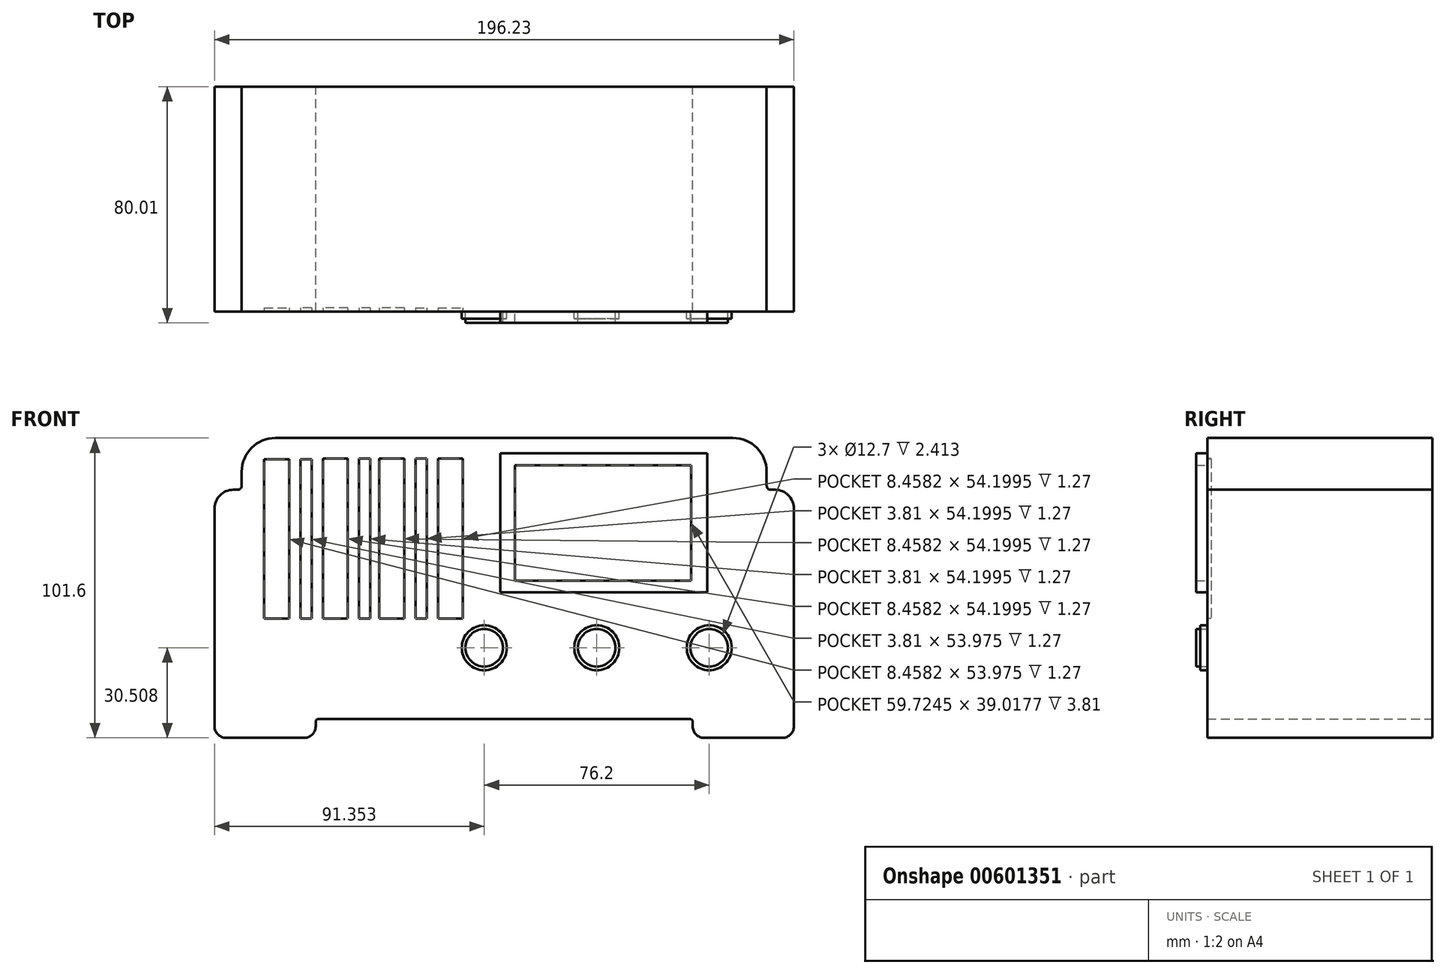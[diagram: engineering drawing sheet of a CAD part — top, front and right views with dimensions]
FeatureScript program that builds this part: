
annotation { "Feature Type Name" : "Feature", "Feature Type Description" : "" }
export const myFeature = defineFeature(function(context is Context, id is Id, definition is map)
    precondition{}
    {
        {
            var Q0;
            Q0=qCreatedBy(makeId("Front.planeOp"),FACE);
            var sketch = newSketch(context, id + "F0", { "sketchPlane" : qUnion([Q0])});
            skLineSegment(sketch, "E0", {"start": v(-84.76, 56.27) * mm, "end": v(93.04, 56.27) * mm});
            skLineSegment(sketch, "E1", {"start": v(-84.76, 56.27) * mm, "end": v(-84.76, -45.33) * mm});
            skLineSegment(sketch, "E2", {"start": v(93.04, 56.27) * mm, "end": v(93.04, -45.33) * mm});
            skLineSegment(sketch, "E3", {"start": v(-84.76, 38.7) * mm, "end": v(-93.97, 38.7) * mm});
            skLineSegment(sketch, "E4", {"start": v(-93.97, 38.7) * mm, "end": v(-93.97, -45.33) * mm});
            skLineSegment(sketch, "E5", {"start": v(-93.97, -45.33) * mm, "end": v(-84.76, -45.33) * mm});
            skLineSegment(sketch, "E6", {"start": v(93.04, 38.7) * mm, "end": v(102.26, 38.7) * mm});
            skLineSegment(sketch, "E7", {"start": v(102.26, 38.7) * mm, "end": v(102.26, -45.33) * mm});
            skLineSegment(sketch, "E8", {"start": v(102.26, -45.33) * mm, "end": v(93.04, -45.33) * mm});
            skLineSegment(sketch, "E9", {"start": v(-84.76, -45.33) * mm, "end": v(-59.72, -45.33) * mm});
            skLineSegment(sketch, "E10", {"start": v(-59.72, -45.33) * mm, "end": v(-59.72, -39) * mm});
            skLineSegment(sketch, "E11", {"start": v(93.04, -45.33) * mm, "end": v(68, -45.33) * mm});
            skLineSegment(sketch, "E12", {"start": v(68, -45.33) * mm, "end": v(68, -39) * mm});
            skLineSegment(sketch, "E13", {"start": v(68, -39) * mm, "end": v(-59.72, -39) * mm});
            skSolve(sketch);
        }
        {
            var Q0;
            Q0 = qSketchRegion(id + "F0", true);
            extrude(context, id + "F1", {"entities" : qUnion([Q0]), "depth" : 76.2 * mm, "offsetDistance" : 25.4 * mm});
        }
        {
            var Q0;
            Q0=makeQuery(id+"F1.opExtrude","CAP_FACE",FACE,{"disambiguationData":[OSD([sQuery(id+"F0.wireOp",EDGE,"E0"),sQuery(id+"F0.wireOp",EDGE,"E1"),sQuery(id+"F0.wireOp",EDGE,"E2"),sQuery(id+"F0.wireOp",EDGE,"E3"),sQuery(id+"F0.wireOp",EDGE,"E4"),sQuery(id+"F0.wireOp",EDGE,"E5"),sQuery(id+"F0.wireOp",EDGE,"E6"),sQuery(id+"F0.wireOp",EDGE,"E7"),sQuery(id+"F0.wireOp",EDGE,"E8"),sQuery(id+"F0.wireOp",EDGE,"E9"),sQuery(id+"F0.wireOp",EDGE,"E10"),sQuery(id+"F0.wireOp",EDGE,"E11"),sQuery(id+"F0.wireOp",EDGE,"E12"),sQuery(id+"F0.wireOp",EDGE,"E13")])],"isStart":false});
            var sketch = newSketch(context, id + "F2", { "sketchPlane" : qUnion([Q0])});
            skCircle(sketch, "E14", {"center": v(-2.62, -14.82) * mm, "radius": 6.35 * mm});
            skCircle(sketch, "E15", {"center": v(35.48, -14.82) * mm, "radius": 6.35 * mm});
            skCircle(sketch, "E16", {"center": v(73.58, -14.82) * mm, "radius": 6.35 * mm});
            skCircle(sketch, "E17", {"center": v(-2.62, -14.82) * mm, "radius": 7.62 * mm});
            skCircle(sketch, "E18", {"center": v(35.48, -14.82) * mm, "radius": 7.62 * mm});
            skCircle(sketch, "E19", {"center": v(73.58, -14.82) * mm, "radius": 7.62 * mm});
            skLineSegment(sketch, "E20", {"start": v(-77.16, 49.02) * mm, "end": v(-77.16, -4.96) * mm});
            skLineSegment(sketch, "E21", {"start": v(-77.16, 49.02) * mm, "end": v(-68.7, 49.02) * mm});
            skLineSegment(sketch, "E22", {"start": v(-68.7, 49.02) * mm, "end": v(-68.7, -4.96) * mm});
            skLineSegment(sketch, "E23", {"start": v(-68.7, -4.96) * mm, "end": v(-77.16, -4.96) * mm});
            skLineSegment(sketch, "E24", {"start": v(-64.9, 49.02) * mm, "end": v(-64.9, -4.96) * mm});
            skLineSegment(sketch, "E25", {"start": v(-64.9, -4.96) * mm, "end": v(-61.08, -4.96) * mm});
            skLineSegment(sketch, "E26", {"start": v(-61.08, -4.96) * mm, "end": v(-61.08, 49.02) * mm});
            skLineSegment(sketch, "E27", {"start": v(-61.08, 49.02) * mm, "end": v(-64.9, 49.02) * mm});
            skLineSegment(sketch, "E28", {"start": v(-57.27, 49.24) * mm, "end": v(-57.27, -4.96) * mm});
            skLineSegment(sketch, "E29", {"start": v(-57.27, -4.96) * mm, "end": v(-48.81, -4.96) * mm});
            skLineSegment(sketch, "E30", {"start": v(-48.81, -4.96) * mm, "end": v(-48.81, 49.24) * mm});
            skLineSegment(sketch, "E31", {"start": v(-48.81, 49.24) * mm, "end": v(-57.27, 49.24) * mm});
            skLineSegment(sketch, "E32", {"start": v(-45, 49.24) * mm, "end": v(-45, -4.96) * mm});
            skLineSegment(sketch, "E33", {"start": v(-45, -4.96) * mm, "end": v(-41.2, -4.96) * mm});
            skLineSegment(sketch, "E34", {"start": v(-41.2, -4.96) * mm, "end": v(-41.2, 49.24) * mm});
            skLineSegment(sketch, "E35", {"start": v(-41.2, 49.24) * mm, "end": v(-45, 49.24) * mm});
            skLineSegment(sketch, "E36", {"start": v(-38.18, 49.24) * mm, "end": v(-38.18, -4.96) * mm});
            skLineSegment(sketch, "E37", {"start": v(-38.18, -4.96) * mm, "end": v(-29.72, -4.96) * mm});
            skLineSegment(sketch, "E38", {"start": v(-29.72, -4.96) * mm, "end": v(-29.72, 49.24) * mm});
            skLineSegment(sketch, "E39", {"start": v(-29.72, 49.24) * mm, "end": v(-38.18, 49.24) * mm});
            skLineSegment(sketch, "E40", {"start": v(-25.9, 49.24) * mm, "end": v(-25.9, -4.96) * mm});
            skLineSegment(sketch, "E41", {"start": v(-25.9, 49.24) * mm, "end": v(-22.1, 49.24) * mm});
            skLineSegment(sketch, "E42", {"start": v(-22.1, 49.24) * mm, "end": v(-22.1, -4.96) * mm});
            skLineSegment(sketch, "E43", {"start": v(-22.1, -4.96) * mm, "end": v(-25.9, -4.96) * mm});
            skLineSegment(sketch, "E44", {"start": v(-18.29, 49.24) * mm, "end": v(-18.29, -4.96) * mm});
            skLineSegment(sketch, "E45", {"start": v(-18.29, 49.24) * mm, "end": v(-9.83, 49.24) * mm});
            skLineSegment(sketch, "E46", {"start": v(-9.83, 49.24) * mm, "end": v(-9.83, -4.96) * mm});
            skLineSegment(sketch, "E47", {"start": v(-9.83, -4.96) * mm, "end": v(-18.29, -4.96) * mm});
            skSolve(sketch);
        }
        {
            var Q0;
            Q0=makeQuery(id+"F2.imprint","IMPRINT",FACE,{"disambiguationData":[TD([[makeQuery(id+"F2.imprint","IMPRINT",EDGE,{"derivedFrom":sQuery(id+"F2.wireOp",EDGE,"E14")}),1.0]])]});
            var Q1;
            Q1=makeQuery(id+"F2.imprint","IMPRINT",FACE,{"disambiguationData":[TD([[makeQuery(id+"F2.imprint","IMPRINT",EDGE,{"derivedFrom":sQuery(id+"F2.wireOp",EDGE,"E15")}),1.0]])]});
            var Q2;
            Q2=makeQuery(id+"F2.imprint","IMPRINT",FACE,{"disambiguationData":[TD([[makeQuery(id+"F2.imprint","IMPRINT",EDGE,{"derivedFrom":sQuery(id+"F2.wireOp",EDGE,"E16")}),1.0]])]});
            extrude(context, id + "F3", {"entities" : qUnion([Q0, Q1, Q2]), "operationType" : NewBodyOperationType.ADD, "depth" : 3.8 * mm, "offsetDistance" : 25.4 * mm});
        }
        {
            var Q0;
            Q0=makeQuery(id+"F2.imprint","IMPRINT",FACE,{"disambiguationData":[TD([[makeQuery(id+"F2.imprint","IMPRINT",EDGE,{"derivedFrom":sQuery(id+"F2.wireOp",EDGE,"E14")}),-1.0]])]});
            var Q1;
            Q1=makeQuery(id+"F2.imprint","IMPRINT",FACE,{"disambiguationData":[TD([[makeQuery(id+"F2.imprint","IMPRINT",EDGE,{"derivedFrom":sQuery(id+"F2.wireOp",EDGE,"E15")}),-1.0]])]});
            var Q2;
            Q2=makeQuery(id+"F2.imprint","IMPRINT",FACE,{"disambiguationData":[TD([[makeQuery(id+"F2.imprint","IMPRINT",EDGE,{"derivedFrom":sQuery(id+"F2.wireOp",EDGE,"E16")}),-1.0]])]});
            var Q3;
            Q3=sQuery(id+"F2.wireOp",EDGE,"E17");
            var Q4;
            Q4=sQuery(id+"F2.wireOp",EDGE,"E18");
            var Q5;
            Q5=sQuery(id+"F2.wireOp",EDGE,"E19");
            extrude(context, id + "F4", {"entities" : qUnion([Q0, Q1, Q2]), "surfaceEntities" : qUnion([Q3, Q4, Q5]), "depth" : 2.41 * mm, "offsetDistance" : 25.4 * mm});
        }
        {
            var Q0;
            Q0=makeQuery(id+"F2.imprint","IMPRINT",FACE,{"disambiguationData":[TD([[makeQuery(id+"F2.imprint","IMPRINT",EDGE,{"derivedFrom":sQuery(id+"F2.wireOp",EDGE,"E20")}),1.0]])]});
            var Q1;
            Q1=makeQuery(id+"F2.imprint","IMPRINT",FACE,{"disambiguationData":[TD([[makeQuery(id+"F2.imprint","IMPRINT",EDGE,{"derivedFrom":sQuery(id+"F2.wireOp",EDGE,"E24")}),1.0]])]});
            var Q2;
            Q2=makeQuery(id+"F2.imprint","IMPRINT",FACE,{"disambiguationData":[TD([[makeQuery(id+"F2.imprint","IMPRINT",EDGE,{"derivedFrom":sQuery(id+"F2.wireOp",EDGE,"E28")}),1.0]])]});
            var Q3;
            Q3=makeQuery(id+"F2.imprint","IMPRINT",FACE,{"disambiguationData":[TD([[makeQuery(id+"F2.imprint","IMPRINT",EDGE,{"derivedFrom":sQuery(id+"F2.wireOp",EDGE,"E32")}),1.0]])]});
            var Q4;
            Q4=makeQuery(id+"F2.imprint","IMPRINT",FACE,{"disambiguationData":[TD([[makeQuery(id+"F2.imprint","IMPRINT",EDGE,{"derivedFrom":sQuery(id+"F2.wireOp",EDGE,"E36")}),1.0]])]});
            var Q5;
            Q5=makeQuery(id+"F2.imprint","IMPRINT",FACE,{"disambiguationData":[TD([[makeQuery(id+"F2.imprint","IMPRINT",EDGE,{"derivedFrom":sQuery(id+"F2.wireOp",EDGE,"E40")}),1.0]])]});
            var Q6;
            Q6=makeQuery(id+"F2.imprint","IMPRINT",FACE,{"disambiguationData":[TD([[makeQuery(id+"F2.imprint","IMPRINT",EDGE,{"derivedFrom":sQuery(id+"F2.wireOp",EDGE,"E44")}),1.0]])]});
            var Q7;
            Q7=sQuery(id+"F2.wireOp",EDGE,"E20");
            var Q8;
            Q8=sQuery(id+"F2.wireOp",EDGE,"E21");
            var Q9;
            Q9=sQuery(id+"F2.wireOp",EDGE,"E22");
            var Q10;
            Q10=sQuery(id+"F2.wireOp",EDGE,"E23");
            var Q11;
            Q11=sQuery(id+"F2.wireOp",EDGE,"E28");
            var Q12;
            Q12=sQuery(id+"F2.wireOp",EDGE,"E29");
            var Q13;
            Q13=sQuery(id+"F2.wireOp",EDGE,"E30");
            var Q14;
            Q14=sQuery(id+"F2.wireOp",EDGE,"E31");
            var Q15;
            Q15=sQuery(id+"F2.wireOp",EDGE,"E37");
            var Q16;
            Q16=sQuery(id+"F2.wireOp",EDGE,"E36");
            var Q17;
            Q17=sQuery(id+"F2.wireOp",EDGE,"E38");
            var Q18;
            Q18=sQuery(id+"F2.wireOp",EDGE,"E39");
            var Q19;
            Q19=sQuery(id+"F2.wireOp",EDGE,"E44");
            var Q20;
            Q20=sQuery(id+"F2.wireOp",EDGE,"E47");
            var Q21;
            Q21=sQuery(id+"F2.wireOp",EDGE,"E45");
            var Q22;
            Q22=sQuery(id+"F2.wireOp",EDGE,"E46");
            extrude(context, id + "F5", {"entities" : qUnion([Q0, Q1, Q2, Q3, Q4, Q5, Q6]), "operationType" : NewBodyOperationType.REMOVE, "surfaceEntities" : qUnion([Q7, Q8, Q9, Q10, Q11, Q12, Q13, Q14, Q15, Q16, Q17, Q18, Q19, Q20, Q21, Q22]), "oppositeDirection" : true, "depth" : 1.27 * mm, "offsetDistance" : 25.4 * mm});
        }
        {
            var Q0;
            Q0=makeQuery(id+"F1.opExtrude","SWEPT_EDGE",EDGE,{"disambiguationData":[OSD([sQuery(id+"F0.wireOp",EDGE,"E6"),sQuery(id+"F0.wireOp",EDGE,"E7")])]});
            var Q1;
            Q1=makeQuery(id+"F1.opExtrude","SWEPT_EDGE",EDGE,{"disambiguationData":[OSD([sQuery(id+"F0.wireOp",EDGE,"E3"),sQuery(id+"F0.wireOp",EDGE,"E4")])]});
            fillet(context, id + "F6", {"entities" : qUnion([Q0, Q1]), "radius" : 6.35 * mm, "tangentPropagation" : true, "allowEdgeOverflow" : false});
        }
        {
            var Q0;
            Q0=makeQuery(id+"F1.opExtrude","SWEPT_EDGE",EDGE,{"disambiguationData":[OSD([sQuery(id+"F0.wireOp",EDGE,"E0"),sQuery(id+"F0.wireOp",EDGE,"E2")])]});
            var Q1;
            Q1=makeQuery(id+"F1.opExtrude","SWEPT_EDGE",EDGE,{"disambiguationData":[OSD([sQuery(id+"F0.wireOp",EDGE,"E0"),sQuery(id+"F0.wireOp",EDGE,"E1")])]});
            fillet(context, id + "F7", {"entities" : qUnion([Q0, Q1]), "radius" : 11.43 * mm, "tangentPropagation" : true, "allowEdgeOverflow" : false});
        }
        {
            var Q0;
            Q0=makeQuery(id+"F1.opExtrude","SWEPT_EDGE",EDGE,{"disambiguationData":[OSD([sQuery(id+"F0.wireOp",EDGE,"E11"),sQuery(id+"F0.wireOp",EDGE,"E12")])]});
            var Q1;
            Q1=makeQuery(id+"F1.opExtrude","SWEPT_EDGE",EDGE,{"disambiguationData":[OSD([sQuery(id+"F0.wireOp",EDGE,"E9"),sQuery(id+"F0.wireOp",EDGE,"E10")])]});
            fillet(context, id + "F8", {"entities" : qUnion([Q0, Q1]), "radius" : 3.8 * mm, "tangentPropagation" : true, "allowEdgeOverflow" : false});
        }
        {
            var Q0;
            Q0=makeQuery(id+"F1.opExtrude","SWEPT_EDGE",EDGE,{"disambiguationData":[OSD([sQuery(id+"F0.wireOp",EDGE,"E7"),sQuery(id+"F0.wireOp",EDGE,"E8")])]});
            var Q1;
            Q1=makeQuery(id+"F1.opExtrude","SWEPT_EDGE",EDGE,{"disambiguationData":[OSD([sQuery(id+"F0.wireOp",EDGE,"E4"),sQuery(id+"F0.wireOp",EDGE,"E5")])]});
            fillet(context, id + "F9", {"entities" : qUnion([Q0, Q1]), "radius" : 3.8 * mm, "tangentPropagation" : true, "allowEdgeOverflow" : false});
        }
        {
            var Q0;
            Q0=makeQuery(id+"F1.opExtrude","SWEPT_EDGE",EDGE,{"disambiguationData":[OSD([sQuery(id+"F0.wireOp",EDGE,"E2"),sQuery(id+"F0.wireOp",EDGE,"E6")])]});
            var Q1;
            Q1=makeQuery(id+"F1.opExtrude","SWEPT_EDGE",EDGE,{"disambiguationData":[OSD([sQuery(id+"F0.wireOp",EDGE,"E1"),sQuery(id+"F0.wireOp",EDGE,"E3")])]});
            fillet(context, id + "F10", {"entities" : qUnion([Q0, Q1]), "radius" : 1.4 * mm, "tangentPropagation" : true, "allowEdgeOverflow" : false});
        }
        {
            var Q0;
            Q0=makeQuery(id+"F1.opExtrude","SWEPT_EDGE",EDGE,{"disambiguationData":[OSD([sQuery(id+"F0.wireOp",EDGE,"E12"),sQuery(id+"F0.wireOp",EDGE,"E13")])]});
            var Q1;
            Q1=makeQuery(id+"F1.opExtrude","SWEPT_EDGE",EDGE,{"disambiguationData":[OSD([sQuery(id+"F0.wireOp",EDGE,"E10"),sQuery(id+"F0.wireOp",EDGE,"E13")])]});
            fillet(context, id + "F11", {"entities" : qUnion([Q0, Q1]), "radius" : 0.89 * mm, "tangentPropagation" : true, "allowEdgeOverflow" : false});
        }
        {
            var Q0;
            Q0=makeQuery(id+"F1.opExtrude","CAP_FACE",FACE,{"disambiguationData":[OSD([sQuery(id+"F0.wireOp",EDGE,"E0"),sQuery(id+"F0.wireOp",EDGE,"E1"),sQuery(id+"F0.wireOp",EDGE,"E2"),sQuery(id+"F0.wireOp",EDGE,"E3"),sQuery(id+"F0.wireOp",EDGE,"E4"),sQuery(id+"F0.wireOp",EDGE,"E5"),sQuery(id+"F0.wireOp",EDGE,"E6"),sQuery(id+"F0.wireOp",EDGE,"E7"),sQuery(id+"F0.wireOp",EDGE,"E8"),sQuery(id+"F0.wireOp",EDGE,"E9"),sQuery(id+"F0.wireOp",EDGE,"E10"),sQuery(id+"F0.wireOp",EDGE,"E11"),sQuery(id+"F0.wireOp",EDGE,"E12"),sQuery(id+"F0.wireOp",EDGE,"E13")])],"isStart":false});
            var sketch = newSketch(context, id + "F12", { "sketchPlane" : qUnion([Q0])});
            skLineSegment(sketch, "E48", {"start": v(2.8, 51.07) * mm, "end": v(2.8, 4) * mm});
            skLineSegment(sketch, "E49", {"start": v(2.8, 4) * mm, "end": v(72.96, 4) * mm});
            skLineSegment(sketch, "E50", {"start": v(72.96, 4) * mm, "end": v(72.96, 51.07) * mm});
            skLineSegment(sketch, "E51", {"start": v(72.96, 51.07) * mm, "end": v(2.8, 51.07) * mm});
            skLineSegment(sketch, "E52", {"start": v(7.76, 46.96) * mm, "end": v(7.76, 7.94) * mm});
            skLineSegment(sketch, "E53", {"start": v(7.76, 7.94) * mm, "end": v(67.49, 7.94) * mm});
            skLineSegment(sketch, "E54", {"start": v(67.49, 7.94) * mm, "end": v(67.49, 46.96) * mm});
            skLineSegment(sketch, "E55", {"start": v(67.49, 46.96) * mm, "end": v(7.76, 46.96) * mm});
            skSolve(sketch);
        }
        {
            var Q0;
            Q0 = qSketchRegion(id + "F12", true);
            extrude(context, id + "F13", {"entities" : qUnion([Q0]), "operationType" : NewBodyOperationType.ADD, "depth" : 3.8 * mm, "offsetDistance" : 25.4 * mm});
        }
    });
